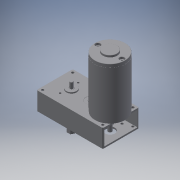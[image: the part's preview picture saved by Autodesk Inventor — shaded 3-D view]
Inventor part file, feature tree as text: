
AUTODESK INVENTOR PART (.ipt)
format: ipt  version: 2016 (Build 200138000, 138)  size: 1,871,360 bytes
history: native  units: in
note: dims shown in document units (in); Inventor stores cm internally (conversion verified against a paired STEP export)
features: other x20, extrude x1, sketch x1
ambient origin geometry x8: Origin, YZ Plane, XZ Plane, XY Plane, X Axis, Y Axis, Z Axis, Center Point
bodies: Solid1 (feature_tree), Solid2 (feature_tree), Solid3 (feature_tree), Solid4 (feature_tree), Solid5 (feature_tree), Solid6 (feature_tree), Solid7 (feature_tree), Solid8 (feature_tree), Solid9 (feature_tree), Solid10 (feature_tree), Solid11 (feature_tree), Solid12 (feature_tree), Solid13 (feature_tree), Solid14 (feature_tree), Solid15 (feature_tree), Solid16 (feature_tree), Solid17 (feature_tree), Solid18 (feature_tree), Solid19 (feature_tree), Solid20 (feature_tree)
feature tree (22):
  other  "TB Hex Output Shaft_3:1"
  extrude  "Extrusion1"  [1 undecoded]
  sketch  "Sketch1"  dims[d0=3.0in d1=0.0in]
  other  "Toughbox-nano-d01_9_8:1"
  other  "50T 20dp 500hex_9:1"
  other  "FR8ZZ Hex Bearing_10:1"
  other  "FR6ZZ Bearing-ab_11:1"
  other  "R6ZZ Bearing_smart_12:1"
  other  "FR6_smart_13:1"
  other  "14T CIM Gear_14:1"
  other  "14T 20dp 375hex_Inch - Spur gear 20DP 14T 14.5PA .568FW ---S14N3.0H2.0L0.25N_15:1"
  other  "50T 20dp 375hex_Inch - Spur gear 20DP 50T 14.5PA .372FW ---S50N3.0H2.0L0.25N_16:1"
  other  "Toughbox Small Hex Shaft_17:1"
  other  "Spacer am-1151_18:1"
  other  "BHCS 10-32 x 0.375 phillips_SBHCSCREW 0.19-32x0.5-HX-C_19:1"
  other  "BHCS 10-32 x 0.375 phillips_SBHCSCREW 0.19-32x0.5-HX-C_20:1"
  other  "5-16 washer_smart_21:1"
  other  "5-16 washer_smart_22:1"
  other  "2mm x 2mm x 10mm Machine Key_smart_23:1"
  other  "8mm_spring_clip am-0033_24:1"
  other  "500-e-klip_smart_2:1"
  other  "CIM motor-1_4:1"
note: 1 required parameter value undecoded (feature->parameter linkage not recoverable at this tier; creation-order binding heuristic only, values carry confidence <= 0.55)
